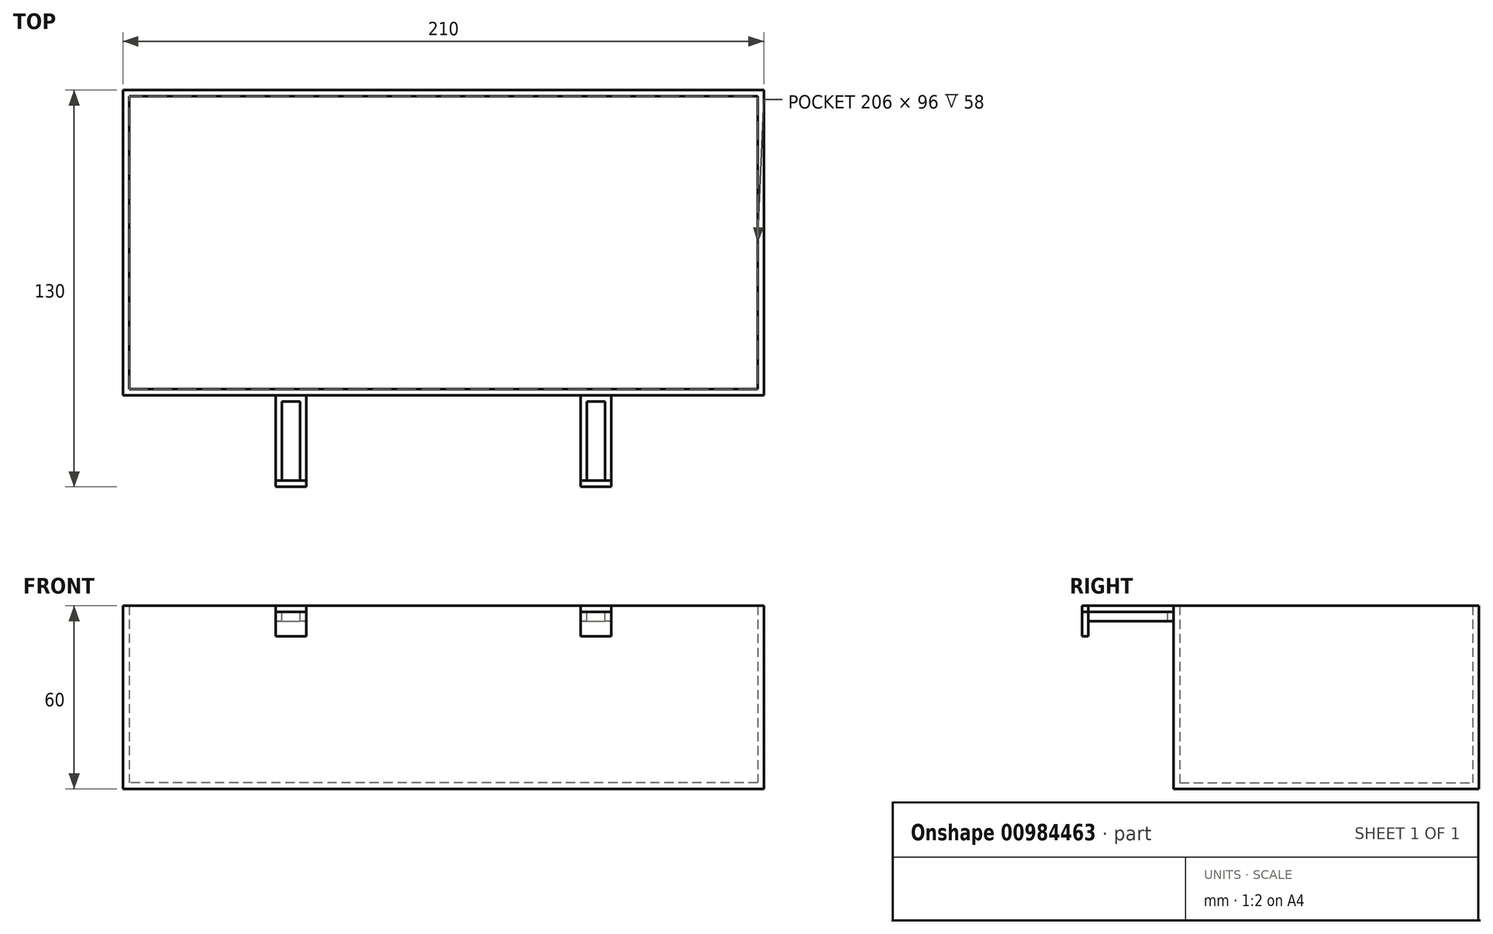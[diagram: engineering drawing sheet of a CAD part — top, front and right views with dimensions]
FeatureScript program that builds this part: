
annotation { "Feature Type Name" : "Feature", "Feature Type Description" : "" }
export const myFeature = defineFeature(function(context is Context, id is Id, definition is map)
    precondition{}
    {
        {
            var Q0;
            Q0=qCreatedBy(makeId("Top.planeOp"),FACE);
            var sketch = newSketch(context, id + "F0", { "sketchPlane" : qUnion([Q0])});
            skLineSegment(sketch, "E0.bottom", {"start": v(-114.72, 50.43) * mm, "end": v(95.28, 50.43) * mm});
            skLineSegment(sketch, "E0.top", {"start": v(-114.72, -49.57) * mm, "end": v(95.28, -49.57) * mm});
            skLineSegment(sketch, "E0.left", {"start": v(-114.72, 50.43) * mm, "end": v(-114.72, -49.57) * mm});
            skLineSegment(sketch, "E0.right", {"start": v(95.28, 50.43) * mm, "end": v(95.28, -49.57) * mm});
            skLineSegment(sketch, "E1.bottom", {"start": v(-112.72, 48.43) * mm, "end": v(93.28, 48.43) * mm});
            skLineSegment(sketch, "E1.top", {"start": v(-112.72, -47.57) * mm, "end": v(93.28, -47.57) * mm});
            skLineSegment(sketch, "E1.left", {"start": v(-112.72, 48.43) * mm, "end": v(-112.72, -47.57) * mm});
            skLineSegment(sketch, "E1.right", {"start": v(93.28, 48.43) * mm, "end": v(93.28, -47.57) * mm});
            skSolve(sketch);
        }
        {
            var Q0;
            Q0=makeQuery(id+"F0.imprint","IMPRINT",FACE,{"disambiguationData":[TD([[makeQuery(id+"F0.imprint","IMPRINT",EDGE,{"derivedFrom":sQuery(id+"F0.wireOp",EDGE,"E1.bottom")}),-1.0]])]});
            var Q1;
            Q1=makeQuery(id+"F0.imprint","IMPRINT",FACE,{"disambiguationData":[TD([[makeQuery(id+"F0.imprint","IMPRINT",EDGE,{"derivedFrom":sQuery(id+"F0.wireOp",EDGE,"E0.bottom")}),-1.0]])]});
            extrude(context, id + "F1", {"entities" : qUnion([Q0, Q1]), "depth" : 2 * mm, "offsetDistance" : 25 * mm});
        }
        {
            var Q0;
            Q0=makeQuery(id+"F0.imprint","IMPRINT",FACE,{"disambiguationData":[TD([[makeQuery(id+"F0.imprint","IMPRINT",EDGE,{"derivedFrom":sQuery(id+"F0.wireOp",EDGE,"E0.bottom")}),-1.0]])]});
            extrude(context, id + "F2", {"entities" : qUnion([Q0]), "operationType" : NewBodyOperationType.ADD, "depth" : 60 * mm, "offsetDistance" : 25 * mm});
        }
        {
            var Q0;
            Q0=makeQuery(id+"F2.opExtrude","CAP_EDGE",EDGE,{"disambiguationData":[OSD([sQuery(id+"F0.wireOp",EDGE,"E0.top")])],"isStart":false});
            cPlane(context, id + "F3", {"entities" : qUnion([Q0]), "cplaneType" : CPlaneType.LINE_ANGLE, "offset" : 25 * mm, "angle" : 90 * degree, "width" : 150 * mm, "height" : 150 * mm});
        }
        {
            var Q0;
            Q0=qCreatedBy(id+"F3.planeOp",FACE);
            var sketch = newSketch(context, id + "F4", { "sketchPlane" : qUnion([Q0])});
            skLineSegment(sketch, "E2.bottom", {"start": v(-64.72, -49.57) * mm, "end": v(-54.72, -49.57) * mm});
            skLineSegment(sketch, "E2.top", {"start": v(-64.72, -79.57) * mm, "end": v(-54.72, -79.57) * mm});
            skLineSegment(sketch, "E2.left", {"start": v(-64.72, -49.57) * mm, "end": v(-64.72, -79.57) * mm});
            skLineSegment(sketch, "E2.right", {"start": v(-54.72, -49.57) * mm, "end": v(-54.72, -79.57) * mm});
            skLineSegment(sketch, "E3.bottom", {"start": v(35.28, -49.57) * mm, "end": v(45.28, -49.57) * mm});
            skLineSegment(sketch, "E3.top", {"start": v(35.28, -79.57) * mm, "end": v(45.28, -79.57) * mm});
            skLineSegment(sketch, "E3.left", {"start": v(35.28, -49.57) * mm, "end": v(35.28, -79.57) * mm});
            skLineSegment(sketch, "E3.right", {"start": v(45.28, -49.57) * mm, "end": v(45.28, -79.57) * mm});
            skLineSegment(sketch, "E4.bottom", {"start": v(-62.72, -51.57) * mm, "end": v(-56.72, -51.57) * mm});
            skLineSegment(sketch, "E4.top", {"start": v(-62.72, -77.57) * mm, "end": v(-56.72, -77.57) * mm});
            skLineSegment(sketch, "E4.left", {"start": v(-62.72, -51.57) * mm, "end": v(-62.72, -77.57) * mm});
            skLineSegment(sketch, "E4.right", {"start": v(-56.72, -51.57) * mm, "end": v(-56.72, -77.57) * mm});
            skLineSegment(sketch, "E5.bottom", {"start": v(37.28, -51.57) * mm, "end": v(43.28, -51.57) * mm});
            skLineSegment(sketch, "E5.top", {"start": v(37.28, -77.57) * mm, "end": v(43.28, -77.57) * mm});
            skLineSegment(sketch, "E5.left", {"start": v(37.28, -51.57) * mm, "end": v(37.28, -77.57) * mm});
            skLineSegment(sketch, "E5.right", {"start": v(43.28, -51.57) * mm, "end": v(43.28, -77.57) * mm});
            skLineSegment(sketch, "E6", {"start": v(-54.72, -77.57) * mm, "end": v(-64.72, -77.57) * mm});
            skLineSegment(sketch, "E7", {"start": v(45.28, -77.57) * mm, "end": v(35.28, -77.57) * mm});
            skSolve(sketch);
        }
        {
            var Q0;
            {var subQ1=sQuery(id+"F4.wireOp",EDGE,"E2.bottom");Q0=makeQuery(id+"F4.imprint","IMPRINT",FACE,{"disambiguationData":[TD([[makeQuery(id+"F4.imprint","IMPRINT",EDGE,{"derivedFrom":subQ1}),-1.0]])]});}
            var Q1;
            Q1=makeQuery(id+"F4.imprint","IMPRINT",FACE,{"disambiguationData":[TD([[makeQuery(id+"F4.imprint","IMPRINT",EDGE,{"derivedFrom":sQuery(id+"F4.wireOp",EDGE,"E4.bottom")}),-1.0]])]});
            var Q2;
            {var subQ1=sQuery(id+"F4.wireOp",EDGE,"E2.top");Q2=makeQuery(id+"F4.imprint","IMPRINT",FACE,{"disambiguationData":[TD([[makeQuery(id+"F4.imprint","IMPRINT",EDGE,{"derivedFrom":subQ1}),1.0]])]});}
            var Q3;
            {var subQ4=sQuery(id+"F4.wireOp",EDGE,"E3.top");Q3=makeQuery(id+"F4.imprint","IMPRINT",FACE,{"disambiguationData":[TD([[makeQuery(id+"F4.imprint","IMPRINT",EDGE,{"derivedFrom":subQ4}),1.0]])]});}
            var Q4;
            Q4=makeQuery(id+"F4.imprint","IMPRINT",FACE,{"disambiguationData":[TD([[makeQuery(id+"F4.imprint","IMPRINT",EDGE,{"derivedFrom":sQuery(id+"F4.wireOp",EDGE,"E5.bottom")}),-1.0]])]});
            var Q5;
            {var subQ1=sQuery(id+"F4.wireOp",EDGE,"E3.bottom");Q5=makeQuery(id+"F4.imprint","IMPRINT",FACE,{"disambiguationData":[TD([[makeQuery(id+"F4.imprint","IMPRINT",EDGE,{"derivedFrom":subQ1}),-1.0]])]});}
            extrude(context, id + "F5", {"entities" : qUnion([Q0, Q1, Q2, Q3, Q4, Q5]), "oppositeDirection" : true, "depth" : 2 * mm, "offsetDistance" : 25 * mm});
        }
        {
            var Q0;
            {var subQ1=sQuery(id+"F4.wireOp",EDGE,"E2.top");Q0=makeQuery(id+"F4.imprint","IMPRINT",FACE,{"disambiguationData":[TD([[makeQuery(id+"F4.imprint","IMPRINT",EDGE,{"derivedFrom":subQ1}),1.0]])]});}
            var Q1;
            {var subQ4=sQuery(id+"F4.wireOp",EDGE,"E3.top");Q1=makeQuery(id+"F4.imprint","IMPRINT",FACE,{"disambiguationData":[TD([[makeQuery(id+"F4.imprint","IMPRINT",EDGE,{"derivedFrom":subQ4}),1.0]])]});}
            extrude(context, id + "F6", {"entities" : qUnion([Q0, Q1]), "oppositeDirection" : true, "depth" : 10 * mm, "offsetDistance" : 25 * mm});
        }
        {
            var Q0;
            {var subQ1=sQuery(id+"F4.wireOp",EDGE,"E2.bottom");Q0=makeQuery(id+"F4.imprint","IMPRINT",FACE,{"disambiguationData":[TD([[makeQuery(id+"F4.imprint","IMPRINT",EDGE,{"derivedFrom":subQ1}),-1.0]])]});}
            var Q1;
            {var subQ1=sQuery(id+"F4.wireOp",EDGE,"E3.bottom");Q1=makeQuery(id+"F4.imprint","IMPRINT",FACE,{"disambiguationData":[TD([[makeQuery(id+"F4.imprint","IMPRINT",EDGE,{"derivedFrom":subQ1}),-1.0]])]});}
            extrude(context, id + "F7", {"entities" : qUnion([Q0, Q1]), "oppositeDirection" : true, "depth" : 5 * mm, "offsetDistance" : 25 * mm});
        }
    });
